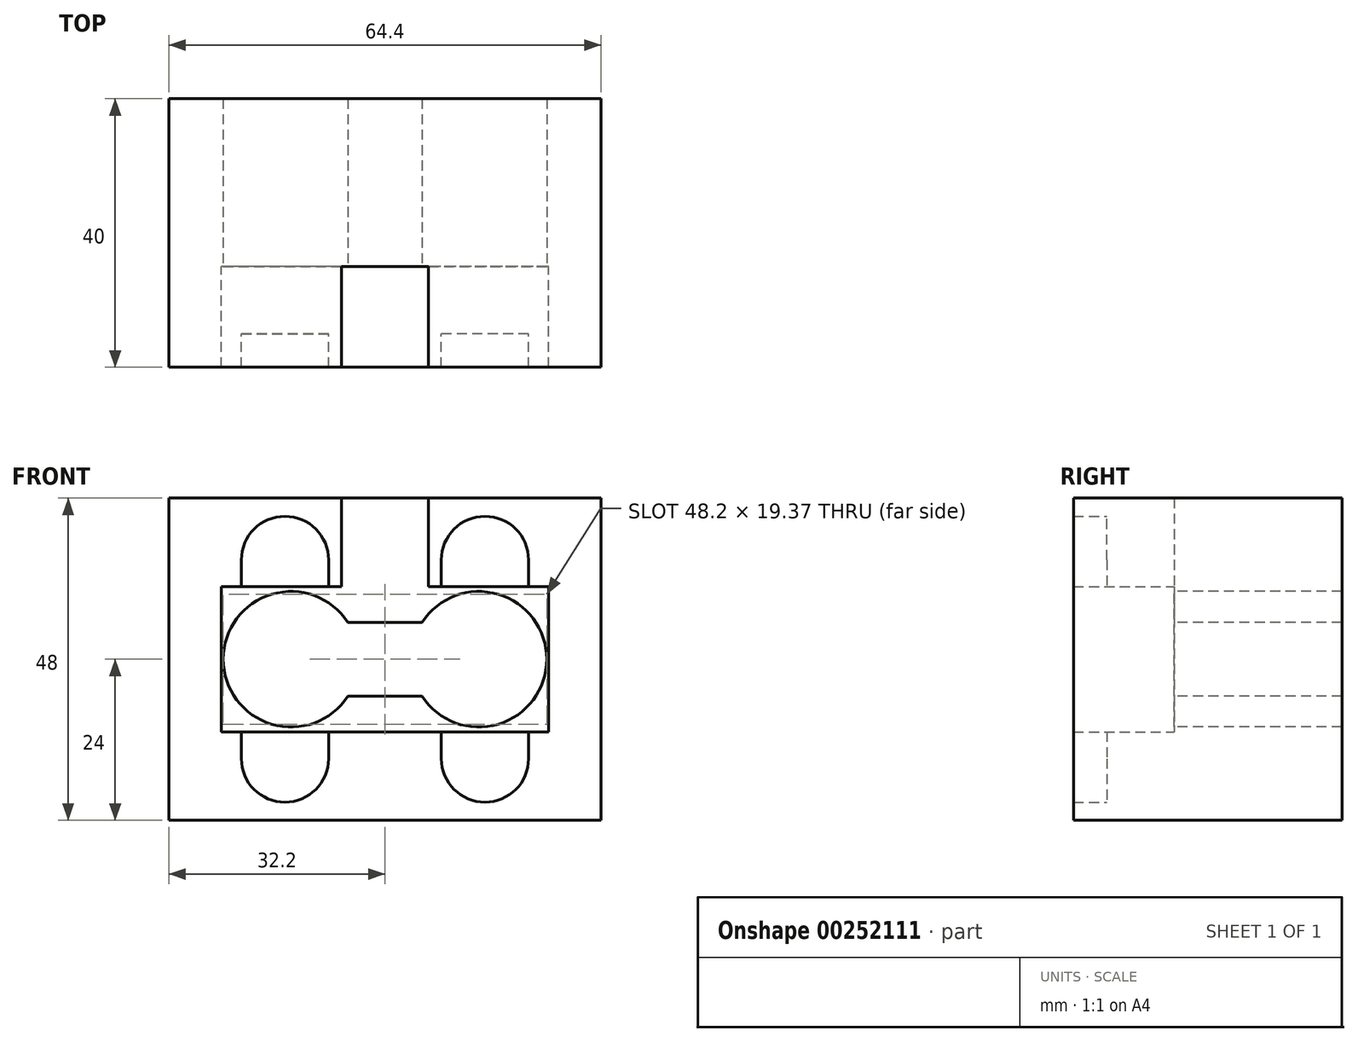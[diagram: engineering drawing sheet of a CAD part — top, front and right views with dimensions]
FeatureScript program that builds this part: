
annotation { "Feature Type Name" : "Feature", "Feature Type Description" : "" }
export const myFeature = defineFeature(function(context is Context, id is Id, definition is map)
    precondition{}
    {
        {
            var Q0;
            Q0=qCreatedBy(makeId("Front.planeOp"),FACE);
            var sketch = newSketch(context, id + "F0", { "sketchPlane" : qUnion([Q0])});
            skLineSegment(sketch, "E0.bottom", {"start": v(32.2, 24) * mm, "end": v(-32.2, 24) * mm});
            skLineSegment(sketch, "E0.top", {"start": v(32.2, -24) * mm, "end": v(-32.2, -24) * mm});
            skLineSegment(sketch, "E0.left", {"start": v(32.2, 24) * mm, "end": v(32.2, -24) * mm});
            skLineSegment(sketch, "E0.right", {"start": v(-32.2, 24) * mm, "end": v(-32.2, -24) * mm});
            skPoint(sketch, "E0.middle", {"position": v(0, 0) * mm});
            skLineSegment(sketch, "E1.bottom", {"start": v(24.4, 10.8) * mm, "end": v(21.4, 10.8) * mm});
            skLineSegment(sketch, "E1.top", {"start": v(24.4, -10.8) * mm, "end": v(21.4, -10.8) * mm});
            skLineSegment(sketch, "E1.left", {"start": v(24.4, 10.8) * mm, "end": v(24.4, -10.8) * mm});
            skLineSegment(sketch, "E1.right", {"start": v(-24.4, 10.8) * mm, "end": v(-24.4, -10.8) * mm});
            skLineSegment(sketch, "E2", {"start": v(-6.5, 24) * mm, "end": v(-6.5, 10.8) * mm});
            skPoint(sketch, "E3", {"position": v(0, 24) * mm});
            skLineSegment(sketch, "E4.MirrorCS", {"start": v(6.5, 24) * mm, "end": v(6.5, 10.8) * mm});
            skLineSegment(sketch, "E5", {"start": v(-21.4, 10.8) * mm, "end": v(-21.4, 14.8) * mm});
            skLineSegment(sketch, "E6", {"start": v(-8.4, 14.8) * mm, "end": v(-8.4, 10.8) * mm});
            skArc(sketch, "E7", {"start": v(-8.4, 14.8) * mm, "mid": v(-14.9, 21.3) * mm, "end": v(-21.4, 14.8) * mm});
            skLineSegment(sketch, "E8.trimOffspring", {"start": v(-21.4, 10.8) * mm, "end": v(-24.4, 10.8) * mm});
            skLineSegment(sketch, "E9.MirrorCS", {"start": v(21.4, 10.8) * mm, "end": v(21.4, 14.8) * mm});
            skArc(sketch, "E10.MirrorCS", {"start": v(8.4, 14.8) * mm, "mid": v(14.9, 21.3) * mm, "end": v(21.4, 14.8) * mm});
            skLineSegment(sketch, "E11.MirrorCS", {"start": v(8.4, 14.8) * mm, "end": v(8.4, 10.8) * mm});
            skLineSegment(sketch, "E12.MirrorCS", {"start": v(-21.4, -10.8) * mm, "end": v(-21.4, -14.8) * mm});
            skArc(sketch, "E13.MirrorCS", {"start": v(-8.4, -14.8) * mm, "mid": v(-14.9, -21.3) * mm, "end": v(-21.4, -14.8) * mm});
            skLineSegment(sketch, "E14.MirrorCS", {"start": v(-8.4, -14.8) * mm, "end": v(-8.4, -10.8) * mm});
            skLineSegment(sketch, "E15.MirrorCS", {"start": v(8.4, -14.8) * mm, "end": v(8.4, -10.8) * mm});
            skArc(sketch, "E16.MirrorCS", {"start": v(8.4, -14.8) * mm, "mid": v(14.9, -21.3) * mm, "end": v(21.4, -14.8) * mm});
            skLineSegment(sketch, "E17.MirrorCS", {"start": v(21.4, -10.8) * mm, "end": v(21.4, -14.8) * mm});
            skLineSegment(sketch, "E18.trimOffspring", {"start": v(8.4, 10.8) * mm, "end": v(6.5, 10.8) * mm});
            skLineSegment(sketch, "E19.trimOffspring", {"start": v(8.4, -10.8) * mm, "end": v(-8.4, -10.8) * mm});
            skLineSegment(sketch, "E20.trimOffspring", {"start": v(-21.4, -10.8) * mm, "end": v(-24.4, -10.8) * mm});
            skLineSegment(sketch, "E21.trimOffspring", {"start": v(-6.5, 10.8) * mm, "end": v(-8.4, 10.8) * mm});
            skSolve(sketch);
        }
        {
            var Q0;
            Q0=makeQuery(id+"F0.imprint","IMPRINT",FACE,{"disambiguationData":[TD([[makeQuery(id+"F0.imprint","IMPRINT",EDGE,{"derivedFrom":sQuery(id+"F0.wireOp",EDGE,"E0.top")}),-1.0]])]});
            extrude(context, id + "F1", {"entities" : qUnion([Q0]), "depth" : 5 * mm});
        }
        {
            var Q0;
            Q0=makeQuery(id+"F1.opExtrude","CAP_FACE",FACE,{"disambiguationData":[OSD([sQuery(id+"F0.wireOp",EDGE,"E0.bottom"),sQuery(id+"F0.wireOp",EDGE,"E0.top"),sQuery(id+"F0.wireOp",EDGE,"E0.left"),sQuery(id+"F0.wireOp",EDGE,"E0.right"),sQuery(id+"F0.wireOp",EDGE,"E1.bottom"),sQuery(id+"F0.wireOp",EDGE,"E1.top"),sQuery(id+"F0.wireOp",EDGE,"E1.left"),sQuery(id+"F0.wireOp",EDGE,"E1.right"),sQuery(id+"F0.wireOp",EDGE,"E2"),sQuery(id+"F0.wireOp",EDGE,"E4.MirrorCS"),sQuery(id+"F0.wireOp",EDGE,"E5"),sQuery(id+"F0.wireOp",EDGE,"E6"),sQuery(id+"F0.wireOp",EDGE,"E7"),sQuery(id+"F0.wireOp",EDGE,"E8.trimOffspring"),sQuery(id+"F0.wireOp",EDGE,"E9.MirrorCS"),sQuery(id+"F0.wireOp",EDGE,"E10.MirrorCS"),sQuery(id+"F0.wireOp",EDGE,"E11.MirrorCS"),sQuery(id+"F0.wireOp",EDGE,"E12.MirrorCS"),sQuery(id+"F0.wireOp",EDGE,"E13.MirrorCS"),sQuery(id+"F0.wireOp",EDGE,"E14.MirrorCS"),sQuery(id+"F0.wireOp",EDGE,"E15.MirrorCS"),sQuery(id+"F0.wireOp",EDGE,"E16.MirrorCS"),sQuery(id+"F0.wireOp",EDGE,"E17.MirrorCS"),sQuery(id+"F0.wireOp",EDGE,"E18.trimOffspring"),sQuery(id+"F0.wireOp",EDGE,"E19.trimOffspring"),sQuery(id+"F0.wireOp",EDGE,"E20.trimOffspring"),sQuery(id+"F0.wireOp",EDGE,"E21.trimOffspring")])],"isStart":true});
            var sketch = newSketch(context, id + "F2", { "sketchPlane" : qUnion([Q0])});
            skLineSegment(sketch, "E22.bottom", {"start": v(24.4, -10.8) * mm, "end": v(-24.4, -10.8) * mm});
            skLineSegment(sketch, "E22.top", {"start": v(24.4, 10.8) * mm, "end": v(-24.4, 10.8) * mm});
            skLineSegment(sketch, "E22.left", {"start": v(24.4, -10.8) * mm, "end": v(24.4, 10.8) * mm});
            skLineSegment(sketch, "E22.right", {"start": v(-24.4, -10.8) * mm, "end": v(-24.4, 10.8) * mm});
            skPoint(sketch, "E22.middle", {"position": v(0, 0) * mm});
            skLineSegment(sketch, "E23.bottom", {"start": v(-32.2, 24) * mm, "end": v(32.2, 24) * mm});
            skLineSegment(sketch, "E23.top", {"start": v(-32.2, -24) * mm, "end": v(32.2, -24) * mm});
            skLineSegment(sketch, "E23.left", {"start": v(-32.2, 24) * mm, "end": v(-32.2, -24) * mm});
            skLineSegment(sketch, "E23.right", {"start": v(32.2, 24) * mm, "end": v(32.2, -24) * mm});
            skLineSegment(sketch, "E24", {"start": v(6.5, 10.8) * mm, "end": v(6.5, 24) * mm});
            skLineSegment(sketch, "E25", {"start": v(-6.5, 10.8) * mm, "end": v(-6.5, 24) * mm});
            skSolve(sketch);
        }
        {
            var Q0;
            {var subQ12=sQuery(id+"F2.wireOp",EDGE,"E22.left");Q0=makeQuery(id+"F2.imprint","IMPRINT",FACE,{"disambiguationData":[TD([[makeQuery(id+"F2.imprint","IMPRINT",EDGE,{"derivedFrom":subQ12}),1.0]])]});}
            var Q1;
            {var subQ1=makeQuery(id+"F1.opExtrude","CAP_EDGE",EDGE,{"disambiguationData":[OSD([sQuery(id+"F0.wireOp",EDGE,"E12.MirrorCS")])],"isStart":true});Q1=makeQuery(id+"F2.imprint","IMPRINT",FACE,{"disambiguationData":[TD([[makeQuery(id+"F2.imprint","IMPRINT",EDGE,{"derivedFrom":subQ1}),-1.0]])]});}
            var Q2;
            {var subQ2=makeQuery(id+"F1.opExtrude","CAP_EDGE",EDGE,{"disambiguationData":[OSD([sQuery(id+"F0.wireOp",EDGE,"E15.MirrorCS")])],"isStart":true});Q2=makeQuery(id+"F2.imprint","IMPRINT",FACE,{"disambiguationData":[TD([[makeQuery(id+"F2.imprint","IMPRINT",EDGE,{"derivedFrom":subQ2}),1.0]])]});}
            var Q3;
            {var subQ1=makeQuery(id+"F1.opExtrude","CAP_EDGE",EDGE,{"disambiguationData":[OSD([sQuery(id+"F0.wireOp",EDGE,"E5")])],"isStart":true});Q3=makeQuery(id+"F2.imprint","IMPRINT",FACE,{"disambiguationData":[TD([[makeQuery(id+"F2.imprint","IMPRINT",EDGE,{"derivedFrom":subQ1}),1.0]])]});}
            var Q4;
            {var subQ1=makeQuery(id+"F1.opExtrude","CAP_EDGE",EDGE,{"disambiguationData":[OSD([sQuery(id+"F0.wireOp",EDGE,"E9.MirrorCS")])],"isStart":true});Q4=makeQuery(id+"F2.imprint","IMPRINT",FACE,{"disambiguationData":[TD([[makeQuery(id+"F2.imprint","IMPRINT",EDGE,{"derivedFrom":subQ1}),-1.0]])]});}
            extrude(context, id + "F3", {"entities" : qUnion([Q0, Q1, Q2, Q3, Q4]), "operationType" : NewBodyOperationType.ADD, "depth" : 10 * mm});
        }
        {
            var Q0;
            Q0=makeQuery(id+"F3.opExtrude","CAP_FACE",FACE,{"disambiguationData":[OSD([sQuery(id+"F2.wireOp",EDGE,"E22.bottom"),sQuery(id+"F2.wireOp",EDGE,"E22.top"),sQuery(id+"F2.wireOp",EDGE,"E22.left"),sQuery(id+"F2.wireOp",EDGE,"E22.right"),sQuery(id+"F2.wireOp",EDGE,"E23.bottom"),sQuery(id+"F2.wireOp",EDGE,"E23.top"),sQuery(id+"F2.wireOp",EDGE,"E23.left"),sQuery(id+"F2.wireOp",EDGE,"E23.right"),sQuery(id+"F2.wireOp",EDGE,"E24"),sQuery(id+"F2.wireOp",EDGE,"E25")])],"isStart":false});
            var sketch = newSketch(context, id + "F4", { "sketchPlane" : qUnion([Q0])});
            skCircle(sketch, "E26", {"center": v(14, 0) * mm, "radius": 10.1 * mm});
            skLineSegment(sketch, "E27", {"start": v(5.53, -5.5) * mm, "end": v(0, -5.5) * mm});
            skLineSegment(sketch, "E28.MirrorCS", {"start": v(5.53, 5.5) * mm, "end": v(0, 5.5) * mm});
            skCircle(sketch, "E29.MirrorC", {"center": v(-14, 0) * mm, "radius": 10.1 * mm});
            skLineSegment(sketch, "E30.MirrorCS", {"start": v(-5.53, -5.5) * mm, "end": v(0, -5.5) * mm});
            skLineSegment(sketch, "E31.MirrorCS", {"start": v(-5.53, 5.5) * mm, "end": v(0, 5.5) * mm});
            skLineSegment(sketch, "E32.bottom", {"start": v(32.2, 24) * mm, "end": v(-32.2, 24) * mm});
            skLineSegment(sketch, "E32.top", {"start": v(32.2, -24) * mm, "end": v(-32.2, -24) * mm});
            skLineSegment(sketch, "E32.left", {"start": v(32.2, 24) * mm, "end": v(32.2, -24) * mm});
            skLineSegment(sketch, "E32.right", {"start": v(-32.2, 24) * mm, "end": v(-32.2, -24) * mm});
            skPoint(sketch, "E32.middle", {"position": v(0, 0) * mm});
            skSolve(sketch);
        }
        {
            var Q0;
            Q0=makeQuery(id+"F4.imprint","IMPRINT",FACE,{"disambiguationData":[TD([[makeQuery(id+"F4.imprint","IMPRINT",EDGE,{"derivedFrom":sQuery(id+"F4.wireOp",EDGE,"E32.top")}),1.0]])]});
            var Q1;
            {var subQ10=sQuery(id+"F4.wireOp",EDGE,"E27");Q1=makeQuery(id+"F4.imprint","IMPRINT",FACE,{"disambiguationData":[TD([[makeQuery(id+"F4.imprint","IMPRINT",EDGE,{"derivedFrom":subQ10}),1.0]])]});}
            extrude(context, id + "F5", {"entities" : qUnion([Q0, Q1]), "operationType" : NewBodyOperationType.ADD, "depth" : 25 * mm});
        }
    });
